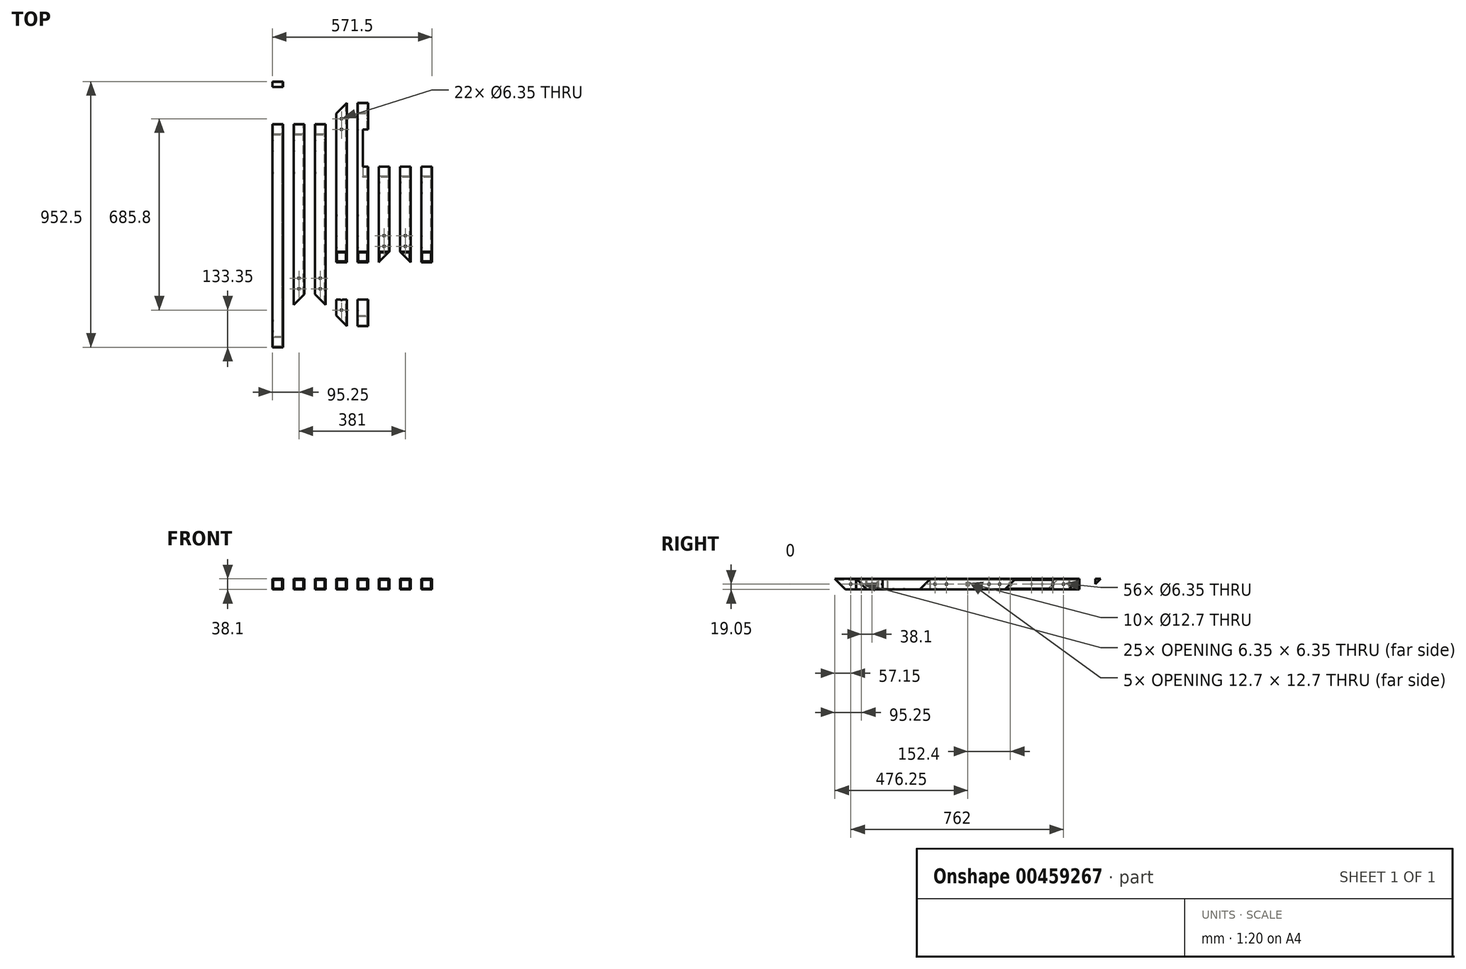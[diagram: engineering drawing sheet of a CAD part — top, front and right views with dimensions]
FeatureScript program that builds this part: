
annotation { "Feature Type Name" : "Feature", "Feature Type Description" : "" }
export const myFeature = defineFeature(function(context is Context, id is Id, definition is map)
    precondition{}
    {
        {
            var Q0;
            Q0=qCreatedBy(makeId("Front.planeOp"),FACE);
            var sketch = newSketch(context, id + "F0", { "sketchPlane" : qUnion([Q0])});
            skLineSegment(sketch, "E0.bottom", {"start": v(19.05, 19.05) * mm, "end": v(-19.05, 19.05) * mm});
            skLineSegment(sketch, "E0.top", {"start": v(19.05, -19.05) * mm, "end": v(-19.05, -19.05) * mm});
            skLineSegment(sketch, "E0.left", {"start": v(19.05, 19.05) * mm, "end": v(19.05, -19.05) * mm});
            skLineSegment(sketch, "E0.right", {"start": v(-19.05, 19.05) * mm, "end": v(-19.05, -19.05) * mm});
            skPoint(sketch, "E0.middle", {"position": v(0, 0) * mm});
            skLineSegment(sketch, "E1.bottom", {"start": v(15.88, -15.88) * mm, "end": v(-15.87, -15.88) * mm});
            skLineSegment(sketch, "E1.top", {"start": v(15.87, 15.88) * mm, "end": v(-15.88, 15.87) * mm});
            skLineSegment(sketch, "E1.left", {"start": v(15.88, -15.88) * mm, "end": v(15.87, 15.88) * mm});
            skLineSegment(sketch, "E1.right", {"start": v(-15.87, -15.88) * mm, "end": v(-15.88, 15.87) * mm});
            skSolve(sketch);
        }
        {
            var Q0;
            Q0=makeQuery(id+"F0.imprint","IMPRINT",FACE,{"disambiguationData":[TD([[makeQuery(id+"F0.imprint","IMPRINT",EDGE,{"derivedFrom":sQuery(id+"F0.wireOp",EDGE,"E0.bottom")}),1.0]])]});
            extrude(context, id + "F1", {"entities" : qUnion([Q0]), "depth" : 914.4 * mm, "symmetric" : true});
        }
        {
            var Q0;
            Q0=qCreatedBy(makeId("Right.planeOp"),FACE);
            var sketch = newSketch(context, id + "F2", { "sketchPlane" : qUnion([Q0])});
            skCircle(sketch, "E2", {"center": v(0, 0) * mm, "radius": 6.35 * mm});
            skLineSegment(sketch, "E3", {"start": v(-381, 0) * mm, "end": v(-457.2, 76.2) * mm});
            skLineSegment(sketch, "E4", {"start": v(-457.2, 76.2) * mm, "end": v(-558.8, 76.2) * mm});
            skLineSegment(sketch, "E5", {"start": v(-558.8, 76.2) * mm, "end": v(-558.8, -76.2) * mm});
            skLineSegment(sketch, "E6", {"start": v(-558.8, -76.2) * mm, "end": v(-304.8, -76.2) * mm});
            skLineSegment(sketch, "E7", {"start": v(-304.8, -76.2) * mm, "end": v(-381, 0) * mm});
            skCircle(sketch, "E8", {"center": v(-304.8, 0) * mm, "radius": 3.18 * mm});
            skCircle(sketch, "E9", {"center": v(-342.9, 0) * mm, "radius": 3.18 * mm});
            skCircle(sketch, "E10.MirrorC", {"center": v(342.9, 0) * mm, "radius": 3.18 * mm});
            skCircle(sketch, "E11.MirrorC", {"center": v(304.8, 0) * mm, "radius": 3.18 * mm});
            skLineSegment(sketch, "E12.MirrorCS", {"start": v(558.8, -76.2) * mm, "end": v(304.8, -76.2) * mm});
            skLineSegment(sketch, "E13.MirrorCS", {"start": v(558.8, 76.2) * mm, "end": v(558.8, -76.2) * mm});
            skLineSegment(sketch, "E14.MirrorCS", {"start": v(457.2, 76.2) * mm, "end": v(558.8, 76.2) * mm});
            skLineSegment(sketch, "E15.MirrorCS", {"start": v(304.8, -76.2) * mm, "end": v(381, 0) * mm});
            skLineSegment(sketch, "E16.MirrorCS", {"start": v(381, 0) * mm, "end": v(457.2, 76.2) * mm});
            skSolve(sketch);
        }
        {
            var Q0;
            Q0 = qSketchRegion(id + "F2", true);
            extrude(context, id + "F3", {"entities" : qUnion([Q0]), "operationType" : NewBodyOperationType.REMOVE, "oppositeDirection" : true, "depth" : 152.4 * mm, "symmetric" : true});
        }
        {
            var Q0;
            Q0=qCreatedBy(makeId("Front.planeOp"),FACE);
            var sketch = newSketch(context, id + "F4", { "sketchPlane" : qUnion([Q0])});
            skLineSegment(sketch, "E17.bottom", {"start": v(-57.15, 19.05) * mm, "end": v(-95.25, 19.05) * mm});
            skLineSegment(sketch, "E17.top", {"start": v(-57.15, -19.05) * mm, "end": v(-95.25, -19.05) * mm});
            skLineSegment(sketch, "E17.left", {"start": v(-57.15, 19.05) * mm, "end": v(-57.15, -19.05) * mm});
            skLineSegment(sketch, "E17.right", {"start": v(-95.25, 19.05) * mm, "end": v(-95.25, -19.05) * mm});
            skPoint(sketch, "E17.middle", {"position": v(-76.2, 0) * mm});
            skLineSegment(sketch, "E18.bottom", {"start": v(-60.33, -15.88) * mm, "end": v(-92.08, -15.88) * mm});
            skLineSegment(sketch, "E18.top", {"start": v(-60.33, 15.87) * mm, "end": v(-92.08, 15.88) * mm});
            skLineSegment(sketch, "E18.left", {"start": v(-60.33, -15.88) * mm, "end": v(-60.33, 15.87) * mm});
            skLineSegment(sketch, "E18.right", {"start": v(-92.08, -15.88) * mm, "end": v(-92.08, 15.88) * mm});
            skSolve(sketch);
        }
        {
            var Q0;
            Q0 = qSketchRegion(id + "F4", true);
            extrude(context, id + "F5", {"entities" : qUnion([Q0]), "depth" : 914.4 * mm, "symmetric" : true});
        }
        {
            var Q0;
            Q0=makeQuery(id+"F5.opExtrude","SWEPT_FACE",FACE,{"disambiguationData":[OSD([sQuery(id+"F4.wireOp",EDGE,"E17.left")])]});
            var sketch = newSketch(context, id + "F6", { "sketchPlane" : qUnion([Q0])});
            skCircle(sketch, "E19", {"center": v(0, 0) * mm, "radius": 6.35 * mm});
            skSolve(sketch);
        }
        {
            var Q0;
            Q0 = qSketchRegion(id + "F6", true);
            extrude(context, id + "F7", {"entities" : qUnion([Q0]), "operationType" : NewBodyOperationType.REMOVE, "endBound" : BoundingType.THROUGH_ALL, "oppositeDirection" : true, "depth" : 25.4 * mm});
        }
        {
            var Q0;
            Q0=makeQuery(id+"F5.opExtrude","SWEPT_FACE",FACE,{"disambiguationData":[OSD([sQuery(id+"F4.wireOp",EDGE,"E17.bottom")])]});
            var sketch = newSketch(context, id + "F8", { "sketchPlane" : qUnion([Q0])});
            skLineSegment(sketch, "E20", {"start": v(-76.2, 381) * mm, "end": v(-25.4, 431.8) * mm});
            skLineSegment(sketch, "E21", {"start": v(-25.4, 431.8) * mm, "end": v(-25.4, 533.4) * mm});
            skLineSegment(sketch, "E22", {"start": v(-25.4, 533.4) * mm, "end": v(-127, 533.4) * mm});
            skLineSegment(sketch, "E23", {"start": v(-127, 533.4) * mm, "end": v(-127, 330.2) * mm});
            skLineSegment(sketch, "E24", {"start": v(-127, 330.2) * mm, "end": v(-76.2, 381) * mm});
            skCircle(sketch, "E25", {"center": v(-76.2, 342.9) * mm, "radius": 3.18 * mm});
            skCircle(sketch, "E26", {"center": v(-76.2, 304.8) * mm, "radius": 3.18 * mm});
            skCircle(sketch, "E27.MirrorC", {"center": v(-76.2, -304.8) * mm, "radius": 3.18 * mm});
            skCircle(sketch, "E28.MirrorC", {"center": v(-76.2, -342.9) * mm, "radius": 3.18 * mm});
            skLineSegment(sketch, "E29.MirrorCS", {"start": v(-76.2, -381) * mm, "end": v(-25.4, -431.8) * mm});
            skLineSegment(sketch, "E30.MirrorCS", {"start": v(-127, -330.2) * mm, "end": v(-76.2, -381) * mm});
            skLineSegment(sketch, "E31.MirrorCS", {"start": v(-127, -533.4) * mm, "end": v(-127, -330.2) * mm});
            skLineSegment(sketch, "E32.MirrorCS", {"start": v(-25.4, -431.8) * mm, "end": v(-25.4, -533.4) * mm});
            skLineSegment(sketch, "E33.MirrorCS", {"start": v(-25.4, -533.4) * mm, "end": v(-127, -533.4) * mm});
            skSolve(sketch);
        }
        {
            var Q0;
            Q0 = qSketchRegion(id + "F8", true);
            extrude(context, id + "F9", {"entities" : qUnion([Q0]), "operationType" : NewBodyOperationType.REMOVE, "endBound" : BoundingType.THROUGH_ALL, "oppositeDirection" : true, "depth" : 25.4 * mm});
        }
        {
            var Q0;
            Q0=qCreatedBy(makeId("Front.planeOp"),FACE);
            var sketch = newSketch(context, id + "F10", { "sketchPlane" : qUnion([Q0])});
            skLineSegment(sketch, "E34.bottom", {"start": v(95.25, 19.05) * mm, "end": v(57.15, 19.05) * mm});
            skLineSegment(sketch, "E34.top", {"start": v(95.25, -19.05) * mm, "end": v(57.15, -19.05) * mm});
            skLineSegment(sketch, "E34.left", {"start": v(95.25, 19.05) * mm, "end": v(95.25, -19.05) * mm});
            skLineSegment(sketch, "E34.right", {"start": v(57.15, 19.05) * mm, "end": v(57.15, -19.05) * mm});
            skPoint(sketch, "E34.middle", {"position": v(76.2, 0) * mm});
            skLineSegment(sketch, "E35.bottom", {"start": v(92.08, -15.88) * mm, "end": v(60.33, -15.88) * mm});
            skLineSegment(sketch, "E35.top", {"start": v(92.08, 15.88) * mm, "end": v(60.33, 15.87) * mm});
            skLineSegment(sketch, "E35.left", {"start": v(92.08, -15.88) * mm, "end": v(92.08, 15.88) * mm});
            skLineSegment(sketch, "E35.right", {"start": v(60.33, -15.88) * mm, "end": v(60.32, 15.87) * mm});
            skSolve(sketch);
        }
        {
            var Q0;
            Q0 = qSketchRegion(id + "F10", true);
            extrude(context, id + "F11", {"entities" : qUnion([Q0]), "depth" : 457.2 * mm, "symmetric" : true});
        }
        {
            var Q0;
            Q0=qCreatedBy(makeId("Front.planeOp"),FACE);
            var sketch = newSketch(context, id + "F12", { "sketchPlane" : qUnion([Q0])});
            skLineSegment(sketch, "E36.bottom", {"start": v(171.45, 19.05) * mm, "end": v(133.35, 19.05) * mm});
            skLineSegment(sketch, "E36.top", {"start": v(171.45, -19.05) * mm, "end": v(133.35, -19.05) * mm});
            skLineSegment(sketch, "E36.left", {"start": v(171.45, 19.05) * mm, "end": v(171.45, -19.05) * mm});
            skLineSegment(sketch, "E36.right", {"start": v(133.35, 19.05) * mm, "end": v(133.35, -19.05) * mm});
            skPoint(sketch, "E36.middle", {"position": v(152.4, 0) * mm});
            skLineSegment(sketch, "E37.bottom", {"start": v(168.28, -15.88) * mm, "end": v(136.53, -15.88) * mm});
            skLineSegment(sketch, "E37.top", {"start": v(168.28, 15.87) * mm, "end": v(136.53, 15.87) * mm});
            skLineSegment(sketch, "E37.left", {"start": v(168.28, -15.88) * mm, "end": v(168.28, 15.88) * mm});
            skLineSegment(sketch, "E37.right", {"start": v(136.53, -15.88) * mm, "end": v(136.53, 15.87) * mm});
            skLineSegment(sketch, "E38.bottom", {"start": v(247.65, 19.05) * mm, "end": v(209.55, 19.05) * mm});
            skLineSegment(sketch, "E38.top", {"start": v(247.65, -19.05) * mm, "end": v(209.55, -19.05) * mm});
            skLineSegment(sketch, "E38.left", {"start": v(247.65, 19.05) * mm, "end": v(247.65, -19.05) * mm});
            skLineSegment(sketch, "E38.right", {"start": v(209.55, 19.05) * mm, "end": v(209.55, -19.05) * mm});
            skPoint(sketch, "E38.middle", {"position": v(228.6, 0) * mm});
            skLineSegment(sketch, "E39.bottom", {"start": v(244.48, -15.88) * mm, "end": v(212.73, -15.88) * mm});
            skLineSegment(sketch, "E39.top", {"start": v(244.48, 15.87) * mm, "end": v(212.73, 15.87) * mm});
            skLineSegment(sketch, "E39.left", {"start": v(244.48, -15.88) * mm, "end": v(244.48, 15.88) * mm});
            skLineSegment(sketch, "E39.right", {"start": v(212.73, -15.88) * mm, "end": v(212.73, 15.87) * mm});
            skSolve(sketch);
        }
        {
            var Q0;
            Q0 = qSketchRegion(id + "F12", true);
            extrude(context, id + "F13", {"entities" : qUnion([Q0]), "depth" : 457.2 * mm, "symmetric" : true});
        }
        {
            var Q0;
            Q0=qCreatedBy(makeId("Right.planeOp"),FACE);
            var sketch = newSketch(context, id + "F14", { "sketchPlane" : qUnion([Q0])});
            skLineSegment(sketch, "E40", {"start": v(152.4, 0) * mm, "end": v(203.2, 50.8) * mm});
            skLineSegment(sketch, "E41", {"start": v(203.2, 50.8) * mm, "end": v(304.8, 50.8) * mm});
            skLineSegment(sketch, "E42", {"start": v(304.8, 50.8) * mm, "end": v(304.8, -50.8) * mm});
            skLineSegment(sketch, "E43", {"start": v(304.8, -50.8) * mm, "end": v(101.6, -50.8) * mm});
            skLineSegment(sketch, "E44", {"start": v(101.6, -50.8) * mm, "end": v(152.4, 0) * mm});
            skCircle(sketch, "E45", {"center": v(76.2, 0) * mm, "radius": 3.18 * mm});
            skCircle(sketch, "E46", {"center": v(114.3, 0) * mm, "radius": 3.18 * mm});
            skSolve(sketch);
        }
        {
            var Q0;
            Q0 = qSketchRegion(id + "F14", true);
            extrude(context, id + "F15", {"entities" : qUnion([Q0]), "operationType" : NewBodyOperationType.REMOVE, "endBound" : BoundingType.THROUGH_ALL, "depth" : 25.4 * mm});
        }
        {
            var Q0;
            Q0=makeQuery(id+"F11.opExtrude","SWEPT_FACE",FACE,{"disambiguationData":[OSD([sQuery(id+"F10.wireOp",EDGE,"E34.bottom")])]});
            var sketch = newSketch(context, id + "F16", { "sketchPlane" : qUnion([Q0])});
            skLineSegment(sketch, "E47", {"start": v(76.2, -152.4) * mm, "end": v(25.4, -203.2) * mm});
            skLineSegment(sketch, "E48", {"start": v(25.4, -203.2) * mm, "end": v(25.4, -304.8) * mm});
            skLineSegment(sketch, "E49", {"start": v(25.4, -304.8) * mm, "end": v(127, -304.8) * mm});
            skLineSegment(sketch, "E50", {"start": v(127, -304.8) * mm, "end": v(127, -101.6) * mm});
            skLineSegment(sketch, "E51", {"start": v(127, -101.6) * mm, "end": v(76.2, -152.4) * mm});
            skCircle(sketch, "E52", {"center": v(76.2, -76.2) * mm, "radius": 3.18 * mm});
            skCircle(sketch, "E53", {"center": v(76.2, -114.3) * mm, "radius": 3.18 * mm});
            skSolve(sketch);
        }
        {
            var Q0;
            Q0 = qSketchRegion(id + "F16", true);
            extrude(context, id + "F17", {"entities" : qUnion([Q0]), "operationType" : NewBodyOperationType.REMOVE, "endBound" : BoundingType.THROUGH_ALL, "oppositeDirection" : true, "depth" : 25.4 * mm});
        }
        {
            var Q0;
            Q0=makeQuery(id+"F13.opExtrude","SWEPT_FACE",FACE,{"disambiguationData":[OSD([sQuery(id+"F12.wireOp",EDGE,"E36.bottom")])]});
            var sketch = newSketch(context, id + "F18", { "sketchPlane" : qUnion([Q0])});
            skLineSegment(sketch, "E54", {"start": v(152.4, -152.4) * mm, "end": v(101.6, -101.6) * mm});
            skLineSegment(sketch, "E55", {"start": v(101.6, -101.6) * mm, "end": v(101.6, -304.8) * mm});
            skLineSegment(sketch, "E56", {"start": v(101.6, -304.8) * mm, "end": v(203.2, -304.8) * mm});
            skLineSegment(sketch, "E57", {"start": v(203.2, -304.8) * mm, "end": v(203.2, -203.2) * mm});
            skLineSegment(sketch, "E58", {"start": v(203.2, -203.2) * mm, "end": v(152.4, -152.4) * mm});
            skCircle(sketch, "E59", {"center": v(152.4, -76.2) * mm, "radius": 3.18 * mm});
            skCircle(sketch, "E60", {"center": v(152.4, -114.3) * mm, "radius": 3.18 * mm});
            skSolve(sketch);
        }
        {
            var Q0;
            Q0 = qSketchRegion(id + "F18", true);
            extrude(context, id + "F19", {"entities" : qUnion([Q0]), "operationType" : NewBodyOperationType.REMOVE, "endBound" : BoundingType.THROUGH_ALL, "oppositeDirection" : true, "depth" : 25.4 * mm});
        }
        {
            var Q0;
            Q0=makeQuery(id+"F13.opExtrude","SWEPT_FACE",FACE,{"disambiguationData":[OSD([sQuery(id+"F12.wireOp",EDGE,"E38.left")])]});
            var sketch = newSketch(context, id + "F20", { "sketchPlane" : qUnion([Q0])});
            skLineSegment(sketch, "E61", {"start": v(-101.6, 50.8) * mm, "end": v(-152.4, 0) * mm});
            skLineSegment(sketch, "E62", {"start": v(-101.6, 50.8) * mm, "end": v(-304.8, 50.8) * mm});
            skLineSegment(sketch, "E63", {"start": v(-304.8, 50.8) * mm, "end": v(-304.8, -50.8) * mm});
            skLineSegment(sketch, "E64", {"start": v(-304.8, -50.8) * mm, "end": v(-203.2, -50.8) * mm});
            skLineSegment(sketch, "E65", {"start": v(-152.4, 0) * mm, "end": v(-203.2, -50.8) * mm});
            skCircle(sketch, "E66", {"center": v(-117.47, 0) * mm, "radius": 3.18 * mm});
            skCircle(sketch, "E67", {"center": v(-76.2, 0) * mm, "radius": 3.18 * mm});
            skSolve(sketch);
        }
        {
            var Q0;
            Q0 = qSketchRegion(id + "F20", true);
            extrude(context, id + "F21", {"entities" : qUnion([Q0]), "operationType" : NewBodyOperationType.REMOVE, "endBound" : BoundingType.THROUGH_ALL, "oppositeDirection" : true, "depth" : 25.4 * mm});
        }
        {
            var Q0;
            Q0=qCreatedBy(makeId("Front.planeOp"),FACE);
            var sketch = newSketch(context, id + "F22", { "sketchPlane" : qUnion([Q0])});
            skLineSegment(sketch, "E68.bottom", {"start": v(-133.35, 19.05) * mm, "end": v(-171.45, 19.05) * mm});
            skLineSegment(sketch, "E68.top", {"start": v(-133.35, -19.05) * mm, "end": v(-171.45, -19.05) * mm});
            skLineSegment(sketch, "E68.left", {"start": v(-133.35, 19.05) * mm, "end": v(-133.35, -19.05) * mm});
            skLineSegment(sketch, "E68.right", {"start": v(-171.45, 19.05) * mm, "end": v(-171.45, -19.05) * mm});
            skPoint(sketch, "E68.middle", {"position": v(-152.4, 0) * mm});
            skLineSegment(sketch, "E69.bottom", {"start": v(-136.53, -15.88) * mm, "end": v(-168.28, -15.88) * mm});
            skLineSegment(sketch, "E69.top", {"start": v(-136.53, 15.87) * mm, "end": v(-168.28, 15.88) * mm});
            skLineSegment(sketch, "E69.left", {"start": v(-136.53, -15.88) * mm, "end": v(-136.53, 15.88) * mm});
            skLineSegment(sketch, "E69.right", {"start": v(-168.28, -15.88) * mm, "end": v(-168.28, 15.88) * mm});
            skLineSegment(sketch, "E70.bottom", {"start": v(-209.55, 19.05) * mm, "end": v(-247.65, 19.05) * mm});
            skLineSegment(sketch, "E70.top", {"start": v(-209.55, -19.05) * mm, "end": v(-247.65, -19.05) * mm});
            skLineSegment(sketch, "E70.left", {"start": v(-209.55, 19.05) * mm, "end": v(-209.55, -19.05) * mm});
            skLineSegment(sketch, "E70.right", {"start": v(-247.65, 19.05) * mm, "end": v(-247.65, -19.05) * mm});
            skPoint(sketch, "E70.middle", {"position": v(-228.6, 0) * mm});
            skLineSegment(sketch, "E71.bottom", {"start": v(-212.72, -15.88) * mm, "end": v(-244.47, -15.88) * mm});
            skLineSegment(sketch, "E71.top", {"start": v(-212.72, 15.87) * mm, "end": v(-244.47, 15.87) * mm});
            skLineSegment(sketch, "E71.left", {"start": v(-212.72, -15.88) * mm, "end": v(-212.72, 15.87) * mm});
            skLineSegment(sketch, "E71.right", {"start": v(-244.47, -15.88) * mm, "end": v(-244.47, 15.87) * mm});
            skLineSegment(sketch, "E72.bottom", {"start": v(-361.95, 19.05) * mm, "end": v(-400.05, 19.05) * mm});
            skLineSegment(sketch, "E72.top", {"start": v(-361.95, -19.05) * mm, "end": v(-400.05, -19.05) * mm});
            skLineSegment(sketch, "E72.left", {"start": v(-361.95, 19.05) * mm, "end": v(-361.95, -19.05) * mm});
            skLineSegment(sketch, "E72.right", {"start": v(-400.05, 19.05) * mm, "end": v(-400.05, -19.05) * mm});
            skPoint(sketch, "E72.middle", {"position": v(-381, 0) * mm});
            skLineSegment(sketch, "E73.bottom", {"start": v(-365.13, -15.88) * mm, "end": v(-396.88, -15.88) * mm});
            skLineSegment(sketch, "E73.top", {"start": v(-365.13, 15.87) * mm, "end": v(-396.88, 15.87) * mm});
            skLineSegment(sketch, "E73.left", {"start": v(-365.13, -15.88) * mm, "end": v(-365.13, 15.87) * mm});
            skLineSegment(sketch, "E73.right", {"start": v(-396.88, -15.88) * mm, "end": v(-396.88, 15.87) * mm});
            skLineSegment(sketch, "E74.bottom", {"start": v(-285.75, 19.05) * mm, "end": v(-323.85, 19.05) * mm});
            skLineSegment(sketch, "E74.top", {"start": v(-285.75, -19.05) * mm, "end": v(-323.85, -19.05) * mm});
            skLineSegment(sketch, "E74.left", {"start": v(-285.75, 19.05) * mm, "end": v(-285.75, -19.05) * mm});
            skLineSegment(sketch, "E74.right", {"start": v(-323.85, 19.05) * mm, "end": v(-323.85, -19.05) * mm});
            skPoint(sketch, "E74.middle", {"position": v(-304.8, 0) * mm});
            skLineSegment(sketch, "E75.bottom", {"start": v(-288.93, -15.88) * mm, "end": v(-320.68, -15.88) * mm});
            skLineSegment(sketch, "E75.top", {"start": v(-288.93, 15.87) * mm, "end": v(-320.68, 15.88) * mm});
            skLineSegment(sketch, "E75.left", {"start": v(-288.93, -15.88) * mm, "end": v(-288.93, 15.88) * mm});
            skLineSegment(sketch, "E75.right", {"start": v(-320.68, -15.88) * mm, "end": v(-320.68, 15.88) * mm});
            skSolve(sketch);
        }
        {
            var Q0;
            Q0=makeQuery(id+"F22.imprint","IMPRINT",FACE,{"disambiguationData":[TD([[makeQuery(id+"F22.imprint","IMPRINT",EDGE,{"derivedFrom":sQuery(id+"F22.wireOp",EDGE,"E68.bottom")}),1.0]])]});
            var Q1;
            Q1=makeQuery(id+"F22.imprint","IMPRINT",FACE,{"disambiguationData":[TD([[makeQuery(id+"F22.imprint","IMPRINT",EDGE,{"derivedFrom":sQuery(id+"F22.wireOp",EDGE,"E70.bottom")}),1.0]])]});
            extrude(context, id + "F23", {"entities" : qUnion([Q0, Q1]), "depth" : 711.2 * mm, "symmetric" : true});
        }
        {
            var Q0;
            Q0=makeQuery(id+"F22.imprint","IMPRINT",FACE,{"disambiguationData":[TD([[makeQuery(id+"F22.imprint","IMPRINT",EDGE,{"derivedFrom":sQuery(id+"F22.wireOp",EDGE,"E74.bottom")}),1.0]])]});
            extrude(context, id + "F24", {"entities" : qUnion([Q0]), "depth" : 1016 * mm, "symmetric" : true});
        }
        {
            var Q0;
            Q0=makeQuery(id+"F23.opExtrude","SWEPT_FACE",FACE,{"disambiguationData":[OSD([sQuery(id+"F22.wireOp",EDGE,"E68.left")])]});
            var sketch = newSketch(context, id + "F25", { "sketchPlane" : qUnion([Q0])});
            skLineSegment(sketch, "E76", {"start": v(304.8, 0) * mm, "end": v(355.6, 50.8) * mm});
            skLineSegment(sketch, "E77", {"start": v(355.6, 50.8) * mm, "end": v(457.2, 50.8) * mm});
            skLineSegment(sketch, "E78", {"start": v(457.2, 50.8) * mm, "end": v(457.2, -50.8) * mm});
            skLineSegment(sketch, "E79", {"start": v(457.2, -50.8) * mm, "end": v(254, -50.8) * mm});
            skLineSegment(sketch, "E80", {"start": v(254, -50.8) * mm, "end": v(304.8, 0) * mm});
            skCircle(sketch, "E81", {"center": v(228.6, 0) * mm, "radius": 3.18 * mm});
            skCircle(sketch, "E82", {"center": v(266.7, 0) * mm, "radius": 3.18 * mm});
            skCircle(sketch, "E83", {"center": v(152.4, 0) * mm, "radius": 6.35 * mm});
            skSolve(sketch);
        }
        {
            var Q0;
            Q0 = qSketchRegion(id + "F25", true);
            extrude(context, id + "F26", {"entities" : qUnion([Q0]), "operationType" : NewBodyOperationType.REMOVE, "endBound" : BoundingType.THROUGH_ALL, "oppositeDirection" : true, "depth" : 25.4 * mm});
        }
        {
            var Q0;
            Q0=makeQuery(id+"F24.opExtrude","SWEPT_FACE",FACE,{"disambiguationData":[OSD([sQuery(id+"F22.wireOp",EDGE,"E74.left")])]});
            var sketch = newSketch(context, id + "F27", { "sketchPlane" : qUnion([Q0])});
            skLineSegment(sketch, "E84", {"start": v(457.2, 0) * mm, "end": v(508, 50.8) * mm});
            skLineSegment(sketch, "E85", {"start": v(508, 50.8) * mm, "end": v(609.6, 50.8) * mm});
            skLineSegment(sketch, "E86", {"start": v(609.6, 50.8) * mm, "end": v(609.6, -50.8) * mm});
            skLineSegment(sketch, "E87", {"start": v(609.6, -50.8) * mm, "end": v(406.4, -50.8) * mm});
            skLineSegment(sketch, "E88", {"start": v(406.4, -50.8) * mm, "end": v(457.2, 0) * mm});
            skCircle(sketch, "E89", {"center": v(381, 0) * mm, "radius": 3.18 * mm});
            skCircle(sketch, "E90", {"center": v(419.1, 0) * mm, "radius": 3.18 * mm});
            skSolve(sketch);
        }
        {
            var Q0;
            Q0 = qSketchRegion(id + "F27", true);
            extrude(context, id + "F28", {"entities" : qUnion([Q0]), "operationType" : NewBodyOperationType.REMOVE, "endBound" : BoundingType.THROUGH_ALL, "oppositeDirection" : true, "depth" : 25.4 * mm});
        }
        {
            var Q0;
            Q0=makeQuery(id+"F23.opExtrude","SWEPT_FACE",FACE,{"disambiguationData":[OSD([sQuery(id+"F22.wireOp",EDGE,"E68.bottom")])]});
            var sketch = newSketch(context, id + "F29", { "sketchPlane" : qUnion([Q0])});
            skLineSegment(sketch, "E91", {"start": v(-152.4, -304.8) * mm, "end": v(-203.2, -254) * mm});
            skLineSegment(sketch, "E92", {"start": v(-203.2, -457.2) * mm, "end": v(-203.2, -254) * mm});
            skLineSegment(sketch, "E93", {"start": v(-203.2, -457.2) * mm, "end": v(-101.6, -457.2) * mm});
            skLineSegment(sketch, "E94", {"start": v(-101.6, -355.6) * mm, "end": v(-101.6, -457.2) * mm});
            skLineSegment(sketch, "E95", {"start": v(-101.6, -355.6) * mm, "end": v(-152.4, -304.8) * mm});
            skCircle(sketch, "E96", {"center": v(-152.4, -228.6) * mm, "radius": 3.18 * mm});
            skCircle(sketch, "E97", {"center": v(-152.4, -266.7) * mm, "radius": 3.18 * mm});
            skSolve(sketch);
        }
        {
            var Q0;
            Q0 = qSketchRegion(id + "F29", true);
            extrude(context, id + "F30", {"entities" : qUnion([Q0]), "operationType" : NewBodyOperationType.REMOVE, "endBound" : BoundingType.THROUGH_ALL, "oppositeDirection" : true, "depth" : 25.4 * mm});
        }
        {
            var Q0;
            Q0=makeQuery(id+"F23.opExtrude","SWEPT_FACE",FACE,{"disambiguationData":[OSD([sQuery(id+"F22.wireOp",EDGE,"E70.bottom")])]});
            var sketch = newSketch(context, id + "F31", { "sketchPlane" : qUnion([Q0])});
            skLineSegment(sketch, "E98", {"start": v(-228.6, -304.8) * mm, "end": v(-279.4, -355.6) * mm});
            skLineSegment(sketch, "E99", {"start": v(-279.4, -457.2) * mm, "end": v(-279.4, -355.6) * mm});
            skLineSegment(sketch, "E100", {"start": v(-279.4, -457.2) * mm, "end": v(-177.8, -457.2) * mm});
            skLineSegment(sketch, "E101", {"start": v(-177.8, -254) * mm, "end": v(-177.8, -457.2) * mm});
            skLineSegment(sketch, "E102", {"start": v(-177.8, -254) * mm, "end": v(-228.6, -304.8) * mm});
            skCircle(sketch, "E103", {"center": v(-228.6, -228.6) * mm, "radius": 3.18 * mm});
            skCircle(sketch, "E104", {"center": v(-228.6, -266.7) * mm, "radius": 3.18 * mm});
            skSolve(sketch);
        }
        {
            var Q0;
            Q0 = qSketchRegion(id + "F31", true);
            extrude(context, id + "F32", {"entities" : qUnion([Q0]), "operationType" : NewBodyOperationType.REMOVE, "endBound" : BoundingType.THROUGH_ALL, "oppositeDirection" : true, "depth" : 25.4 * mm});
        }
        {
            var Q0;
            Q0=makeQuery(id+"F24.opExtrude","SWEPT_FACE",FACE,{"disambiguationData":[OSD([sQuery(id+"F22.wireOp",EDGE,"E74.right")])]});
            var sketch = newSketch(context, id + "F33", { "sketchPlane" : qUnion([Q0])});
            skLineSegment(sketch, "E105", {"start": v(457.2, 0) * mm, "end": v(508, 50.8) * mm});
            skLineSegment(sketch, "E106", {"start": v(508, 50.8) * mm, "end": v(609.6, 50.8) * mm});
            skLineSegment(sketch, "E107", {"start": v(609.6, 50.8) * mm, "end": v(609.6, -50.8) * mm});
            skLineSegment(sketch, "E108", {"start": v(609.6, -50.8) * mm, "end": v(406.4, -50.8) * mm});
            skLineSegment(sketch, "E109", {"start": v(406.4, -50.8) * mm, "end": v(457.2, 0) * mm});
            skCircle(sketch, "E110", {"center": v(381, 0) * mm, "radius": 3.18 * mm});
            skCircle(sketch, "E111", {"center": v(419.1, 0) * mm, "radius": 3.18 * mm});
            skSolve(sketch);
        }
        {
            var Q0;
            Q0 = qSketchRegion(id + "F33", true);
            extrude(context, id + "F34", {"entities" : qUnion([Q0]), "operationType" : NewBodyOperationType.REMOVE, "endBound" : BoundingType.THROUGH_ALL, "oppositeDirection" : true, "depth" : 25.4 * mm});
        }
    });
